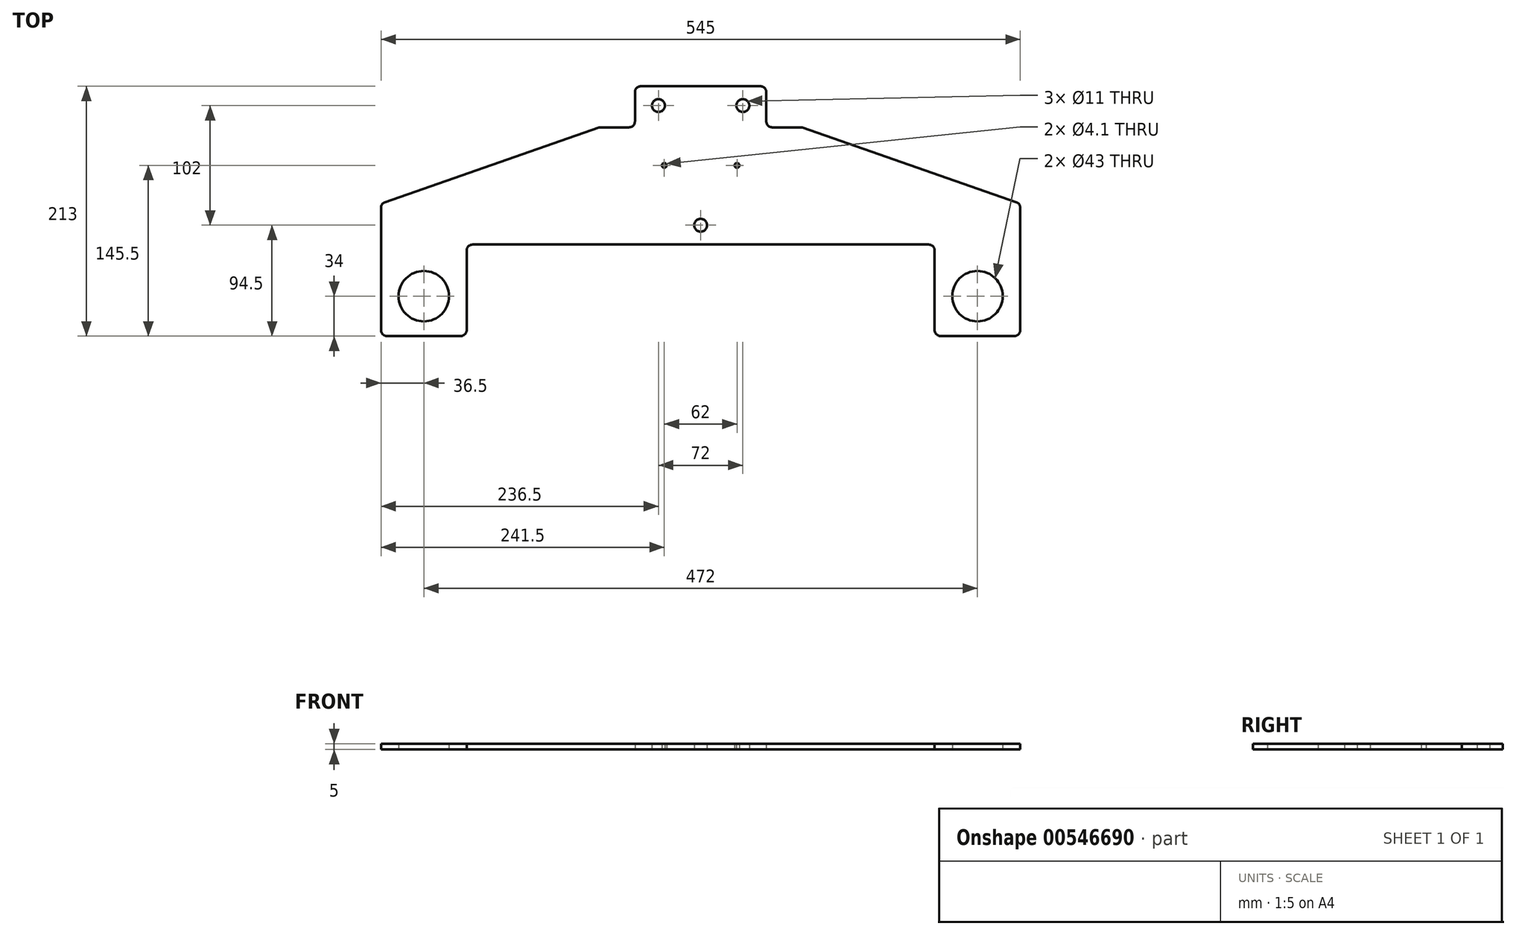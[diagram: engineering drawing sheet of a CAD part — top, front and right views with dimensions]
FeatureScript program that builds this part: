
annotation { "Feature Type Name" : "Feature", "Feature Type Description" : "" }
export const myFeature = defineFeature(function(context is Context, id is Id, definition is map)
    precondition{}
    {
        {
            var Q0;
            Q0=qCreatedBy(makeId("Top.planeOp"),FACE);
            var sketch = newSketch(context, id + "F0", { "sketchPlane" : qUnion([Q0])});
            skLineSegment(sketch, "E0", {"start": v(-86, 50) * mm, "end": v(86, 50) * mm});
            skLineSegment(sketch, "E1", {"start": v(-272.5, -50) * mm, "end": v(272.5, -50) * mm});
            skLineSegment(sketch, "E2", {"start": v(-272.5, -50) * mm, "end": v(-272.5, -128) * mm});
            skLineSegment(sketch, "E3", {"start": v(272.5, -50) * mm, "end": v(272.5, -128) * mm});
            skLineSegment(sketch, "E4", {"start": v(272.5, -128) * mm, "end": v(199.5, -128) * mm});
            skLineSegment(sketch, "E5", {"start": v(199.5, -128) * mm, "end": v(199.5, -50) * mm});
            skLineSegment(sketch, "E6", {"start": v(-272.5, -128) * mm, "end": v(-199.5, -128) * mm});
            skLineSegment(sketch, "E7", {"start": v(-199.5, -128) * mm, "end": v(-199.5, -50) * mm});
            skLineSegment(sketch, "E8", {"start": v(-272.5, -50) * mm, "end": v(-272.5, -15) * mm});
            skLineSegment(sketch, "E9", {"start": v(-272.5, -15) * mm, "end": v(-86, 50) * mm});
            skLineSegment(sketch, "E10", {"start": v(272.5, -50) * mm, "end": v(272.5, -15) * mm});
            skLineSegment(sketch, "E11", {"start": v(86, 50) * mm, "end": v(272.5, -15) * mm});
            skLineSegment(sketch, "E12", {"start": v(56, 50) * mm, "end": v(56, 85) * mm});
            skLineSegment(sketch, "E13", {"start": v(56, 85) * mm, "end": v(-56, 85) * mm});
            skLineSegment(sketch, "E14", {"start": v(-56, 85) * mm, "end": v(-56, 50) * mm});
            skSolve(sketch);
        }
        {
            var Q0;
            Q0=makeQuery(id+"F0.imprint","IMPRINT",FACE,{"disambiguationData":[TD([[makeQuery(id+"F0.imprint","IMPRINT",EDGE,{"derivedFrom":sQuery(id+"F0.wireOp",EDGE,"E0")}),-1.0]])]});
            var Q1;
            {var subQ0=sQuery(id+"F0.wireOp",EDGE,"E2");Q1=makeQuery(id+"F0.imprint","IMPRINT",FACE,{"disambiguationData":[TD([[makeQuery(id+"F0.imprint","IMPRINT",EDGE,{"derivedFrom":subQ0}),1.0]])]});}
            var Q2;
            {var subQ0=sQuery(id+"F0.wireOp",EDGE,"E3");Q2=makeQuery(id+"F0.imprint","IMPRINT",FACE,{"disambiguationData":[TD([[makeQuery(id+"F0.imprint","IMPRINT",EDGE,{"derivedFrom":subQ0}),-1.0]])]});}
            var Q3;
            {var subQ0=sQuery(id+"F0.wireOp",EDGE,"E12");Q3=makeQuery(id+"F0.imprint","IMPRINT",FACE,{"disambiguationData":[TD([[makeQuery(id+"F0.imprint","IMPRINT",EDGE,{"derivedFrom":subQ0}),1.0]])]});}
            extrude(context, id + "F1", {"entities" : qUnion([Q0, Q1, Q2, Q3]), "depth" : 5 * mm});
        }
        {
            var Q0;
            Q0=makeQuery(id+"F1.opExtrude","SWEPT_EDGE",EDGE,{"disambiguationData":[OSD([sQuery(id+"F0.wireOp",EDGE,"E2"),sQuery(id+"F0.wireOp",EDGE,"E6")])]});
            var Q1;
            Q1=makeQuery(id+"F1.opExtrude","SWEPT_EDGE",EDGE,{"disambiguationData":[OSD([sQuery(id+"F0.wireOp",EDGE,"E6"),sQuery(id+"F0.wireOp",EDGE,"E7")])]});
            var Q2;
            Q2=makeQuery(id+"F1.opExtrude","SWEPT_EDGE",EDGE,{"disambiguationData":[OSD([sQuery(id+"F0.wireOp",EDGE,"E4"),sQuery(id+"F0.wireOp",EDGE,"E5")])]});
            var Q3;
            Q3=makeQuery(id+"F1.opExtrude","SWEPT_EDGE",EDGE,{"disambiguationData":[OSD([sQuery(id+"F0.wireOp",EDGE,"E3"),sQuery(id+"F0.wireOp",EDGE,"E4")])]});
            var Q4;
            Q4=makeQuery(id+"F1.opExtrude","SWEPT_EDGE",EDGE,{"disambiguationData":[OSD([sQuery(id+"F0.wireOp",EDGE,"E10"),sQuery(id+"F0.wireOp",EDGE,"E11")])]});
            var Q5;
            Q5=makeQuery(id+"F1.opExtrude","SWEPT_EDGE",EDGE,{"disambiguationData":[OSD([sQuery(id+"F0.wireOp",EDGE,"E8"),sQuery(id+"F0.wireOp",EDGE,"E9")])]});
            var Q6;
            Q6=makeQuery(id+"F1.opExtrude","SWEPT_EDGE",EDGE,{"disambiguationData":[OSD([sQuery(id+"F0.wireOp",EDGE,"E1"),sQuery(id+"F0.wireOp",EDGE,"E7")])]});
            var Q7;
            Q7=makeQuery(id+"F1.opExtrude","SWEPT_EDGE",EDGE,{"disambiguationData":[OSD([sQuery(id+"F0.wireOp",EDGE,"E1"),sQuery(id+"F0.wireOp",EDGE,"E5")])]});
            var Q8;
            Q8=makeQuery(id+"F1.opExtrude","SWEPT_EDGE",EDGE,{"disambiguationData":[OSD([sQuery(id+"F0.wireOp",EDGE,"E0"),sQuery(id+"F0.wireOp",EDGE,"E14")])]});
            var Q9;
            Q9=makeQuery(id+"F1.opExtrude","SWEPT_EDGE",EDGE,{"disambiguationData":[OSD([sQuery(id+"F0.wireOp",EDGE,"E13"),sQuery(id+"F0.wireOp",EDGE,"E14")])]});
            var Q10;
            Q10=makeQuery(id+"F1.opExtrude","SWEPT_EDGE",EDGE,{"disambiguationData":[OSD([sQuery(id+"F0.wireOp",EDGE,"E12"),sQuery(id+"F0.wireOp",EDGE,"E13")])]});
            var Q11;
            Q11=makeQuery(id+"F1.opExtrude","SWEPT_EDGE",EDGE,{"disambiguationData":[OSD([sQuery(id+"F0.wireOp",EDGE,"E0"),sQuery(id+"F0.wireOp",EDGE,"E12")])]});
            fillet(context, id + "F2", {"entities" : qUnion([Q0, Q1, Q2, Q3, Q4, Q5, Q6, Q7, Q8, Q9, Q10, Q11]), "radius" : 5 * mm, "tangentPropagation" : true, "allowEdgeOverflow" : false});
        }
        {
            var Q0;
            Q0=makeQuery(id+"F1.opExtrude","SWEPT_EDGE",EDGE,{"disambiguationData":[OSD([sQuery(id+"F0.wireOp",EDGE,"E0"),sQuery(id+"F0.wireOp",EDGE,"E11")])]});
            var Q1;
            Q1=makeQuery(id+"F1.opExtrude","SWEPT_EDGE",EDGE,{"disambiguationData":[OSD([sQuery(id+"F0.wireOp",EDGE,"E0"),sQuery(id+"F0.wireOp",EDGE,"E9")])]});
            fillet(context, id + "F3", {"entities" : qUnion([Q0, Q1]), "radius" : 5 * mm, "tangentPropagation" : true, "allowEdgeOverflow" : false});
        }
        {
            var Q0;
            Q0=qCreatedBy(makeId("Top.planeOp"),FACE);
            var sketch = newSketch(context, id + "F4", { "sketchPlane" : qUnion([Q0])});
            skCircle(sketch, "E15", {"center": v(-36, 68.5) * mm, "radius": 5.5 * mm});
            skCircle(sketch, "E16", {"center": v(36, 68.5) * mm, "radius": 5.5 * mm});
            skCircle(sketch, "E17", {"center": v(0, -33.5) * mm, "radius": 5.5 * mm});
            skSolve(sketch);
        }
        {
            var Q0;
            Q0=qCreatedBy(makeId("Top.planeOp"),FACE);
            var sketch = newSketch(context, id + "F5", { "sketchPlane" : qUnion([Q0])});
            skCircle(sketch, "E18", {"center": v(-31, 17.5) * mm, "radius": 4.53 * mm});
            skCircle(sketch, "E19", {"center": v(31, 17.5) * mm, "radius": 4.22 * mm});
            skSolve(sketch);
        }
        {
            var Q0;
            Q0=sQuery(id+"F5.wireOp",VERTEX,"E18.center");
            var Q1;
            Q1=sQuery(id+"F5.wireOp",VERTEX,"E19.center");
            var Q2;
            Q2=makeQuery(id+"F1.opExtrude","SWEPT_BODY",BODY,{"disambiguationData":[OSD([sQuery(id+"F0.wireOp",EDGE,"E0"),sQuery(id+"F0.wireOp",EDGE,"E1"),sQuery(id+"F0.wireOp",EDGE,"E2"),sQuery(id+"F0.wireOp",EDGE,"E3"),sQuery(id+"F0.wireOp",EDGE,"E4"),sQuery(id+"F0.wireOp",EDGE,"E5"),sQuery(id+"F0.wireOp",EDGE,"E6"),sQuery(id+"F0.wireOp",EDGE,"E7"),sQuery(id+"F0.wireOp",EDGE,"E8"),sQuery(id+"F0.wireOp",EDGE,"E9"),sQuery(id+"F0.wireOp",EDGE,"E10"),sQuery(id+"F0.wireOp",EDGE,"E11")])]});
            hole(context, id + "F6", {"style" : HoleStyle.SIMPLE, "endStyle" : HoleEndStyle.THROUGH, "oppositeDirection" : true, "holeDiameter" : 4.1 * mm, "tappedDepth" : 12 * mm, "tapClearance" : 3, "locations" : qUnion([Q0, Q1]), "scope" : qUnion([Q2])});
        }
        {
            var Q0;
            Q0=qCreatedBy(makeId("Top.planeOp"),FACE);
            var sketch = newSketch(context, id + "F7", { "sketchPlane" : qUnion([Q0])});
            skCircle(sketch, "E20", {"center": v(-236, -94) * mm, "radius": 11.57 * mm});
            skCircle(sketch, "E21", {"center": v(236, -94) * mm, "radius": 8.32 * mm});
            skSolve(sketch);
        }
        {
            var Q0;
            Q0=sQuery(id+"F7.wireOp",VERTEX,"E20.center");
            var Q1;
            Q1=sQuery(id+"F7.wireOp",VERTEX,"E21.center");
            var Q2;
            Q2=makeQuery(id+"F1.opExtrude","SWEPT_BODY",BODY,{"disambiguationData":[OSD([sQuery(id+"F0.wireOp",EDGE,"E0"),sQuery(id+"F0.wireOp",EDGE,"E1"),sQuery(id+"F0.wireOp",EDGE,"E2"),sQuery(id+"F0.wireOp",EDGE,"E3"),sQuery(id+"F0.wireOp",EDGE,"E4"),sQuery(id+"F0.wireOp",EDGE,"E5"),sQuery(id+"F0.wireOp",EDGE,"E6"),sQuery(id+"F0.wireOp",EDGE,"E7"),sQuery(id+"F0.wireOp",EDGE,"E8"),sQuery(id+"F0.wireOp",EDGE,"E9"),sQuery(id+"F0.wireOp",EDGE,"E10"),sQuery(id+"F0.wireOp",EDGE,"E11")])]});
            hole(context, id + "F8", {"style" : HoleStyle.SIMPLE, "endStyle" : HoleEndStyle.THROUGH, "oppositeDirection" : true, "holeDiameter" : 43 * mm, "tappedDepth" : 12 * mm, "tapClearance" : 3, "locations" : qUnion([Q0, Q1]), "scope" : qUnion([Q2])});
        }
        {
            var Q0;
            Q0=sQuery(id+"F4.wireOp",VERTEX,"E15.center");
            var Q1;
            Q1=sQuery(id+"F4.wireOp",VERTEX,"E16.center");
            var Q2;
            Q2=sQuery(id+"F4.wireOp",VERTEX,"E17.center");
            var Q3;
            Q3=makeQuery(id+"F1.opExtrude","SWEPT_BODY",BODY,{"disambiguationData":[OSD([sQuery(id+"F0.wireOp",EDGE,"E0"),sQuery(id+"F0.wireOp",EDGE,"E1"),sQuery(id+"F0.wireOp",EDGE,"E2"),sQuery(id+"F0.wireOp",EDGE,"E3"),sQuery(id+"F0.wireOp",EDGE,"E4"),sQuery(id+"F0.wireOp",EDGE,"E5"),sQuery(id+"F0.wireOp",EDGE,"E6"),sQuery(id+"F0.wireOp",EDGE,"E7"),sQuery(id+"F0.wireOp",EDGE,"E8"),sQuery(id+"F0.wireOp",EDGE,"E9"),sQuery(id+"F0.wireOp",EDGE,"E10"),sQuery(id+"F0.wireOp",EDGE,"E11"),sQuery(id+"F0.wireOp",EDGE,"E12"),sQuery(id+"F0.wireOp",EDGE,"E13"),sQuery(id+"F0.wireOp",EDGE,"E14")])]});
            hole(context, id + "F9", {"style" : HoleStyle.SIMPLE, "endStyle" : HoleEndStyle.THROUGH, "oppositeDirection" : true, "standardTappedOrClearance" : lookupTablePath({ "standard" : "ISO", "fit" : "Normal", "size" : "M10", "type" : "Clearance" }), "standardBlindInLast" : lookupTablePath({ "fit" : "Standard", "standard" : "ISO", "size" : "M10", "type" : "Clearance" }), "holeDiameter" : 11 * mm, "tappedDepth" : 12 * mm, "tapClearance" : 3, "locations" : qUnion([Q0, Q1, Q2]), "scope" : qUnion([Q3])});
        }
    });
